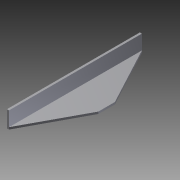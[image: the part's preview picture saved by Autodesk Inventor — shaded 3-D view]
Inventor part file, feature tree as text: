
AUTODESK INVENTOR PART (.ipt)
format: ipt  version: 2012 (Build 160160000, 160)  size: 89,600 bytes
history: native  units: in
note: dims shown in document units (in); Inventor stores cm internally (conversion verified against a paired STEP export)
features: extrude x2, sketch x2
ambient origin geometry x8: Origin, YZ Plane, XZ Plane, XY Plane, X Axis, Y Axis, Z Axis, Center Point
bodies: Solid1 (feature_tree)
feature tree (4):
  extrude  "Extrusion1"  Depth=1.0in
  extrude  "Extrusion4"  Depth=0.125in
  sketch  "Sketch1"  dims[d0=2.0in d1=1.0in]
  sketch  "Sketch2"  dims[d2=0.125in d3=0.125in d4=8.0in d5=0.0in d18=1.0in d19=3.5in d20=3.5in d21=1.0in d22=0.0in]
